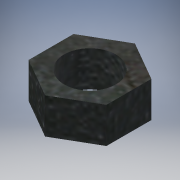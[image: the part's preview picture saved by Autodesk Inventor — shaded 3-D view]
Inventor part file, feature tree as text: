
AUTODESK INVENTOR PART (.ipt)
format: ipt  version: 2016 (Build 200138000, 138)  size: 114,688 bytes
history: native  units: in
note: dims shown in document units (in); Inventor stores cm internally (conversion verified against a paired STEP export)
features: extrude x1, sketch x1
ambient origin geometry x8: Origin, YZ Plane, XZ Plane, XY Plane, X Axis, Y Axis, Z Axis, Center Point
bodies: Solid1 (feature_tree)
feature tree (2):
  extrude  "Extrusion1"  Depth=0.3438in
  sketch  "Sketch1"  dims[d0=0.75in d1=0.5in d2=0.3438in d3=0.0in]
